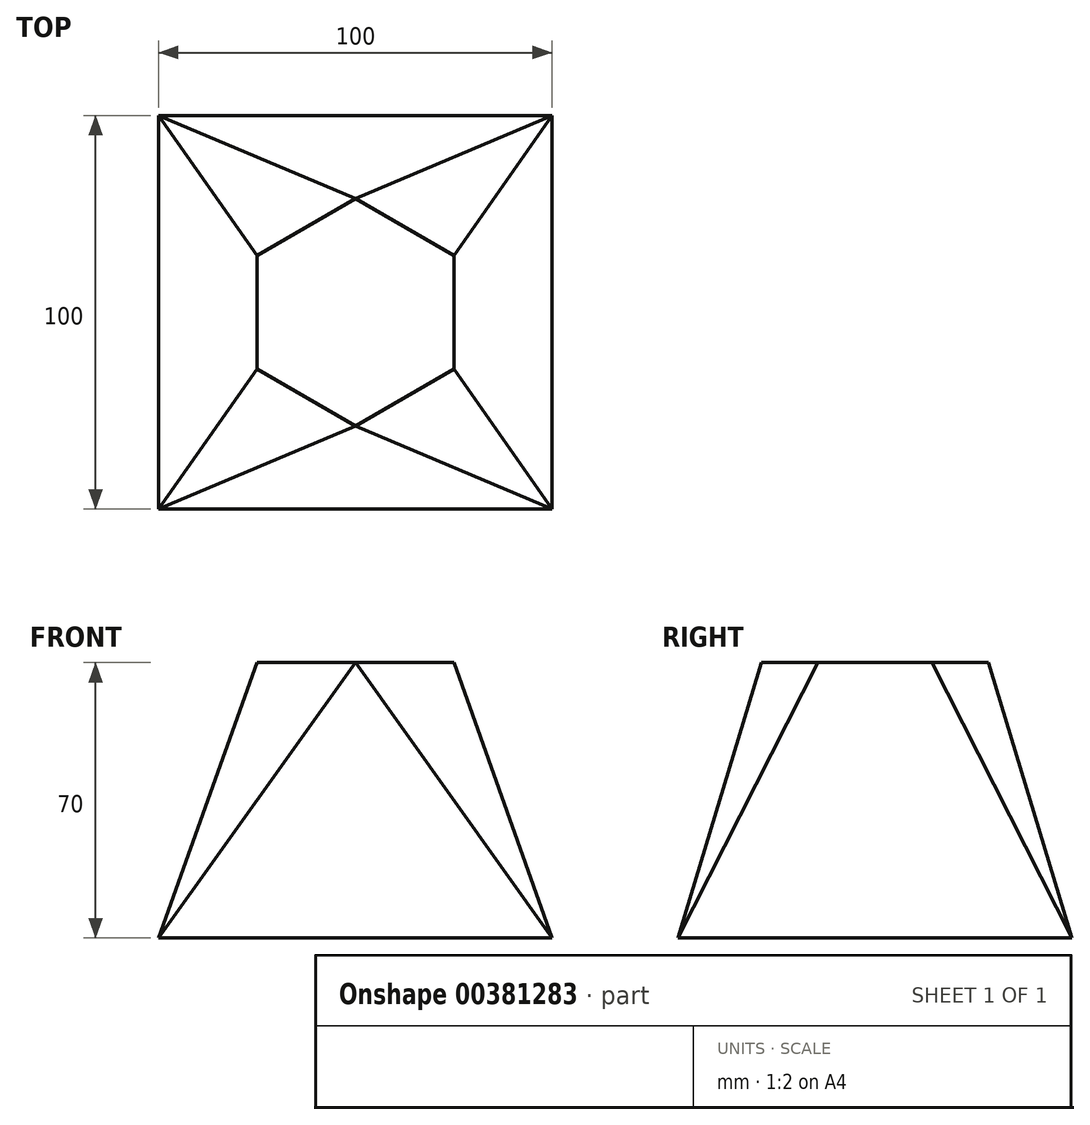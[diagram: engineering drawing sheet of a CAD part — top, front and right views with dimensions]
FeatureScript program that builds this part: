
annotation { "Feature Type Name" : "Feature", "Feature Type Description" : "" }
export const myFeature = defineFeature(function(context is Context, id is Id, definition is map)
    precondition{}
    {
        {
            var Q0;
            Q0=qCreatedBy(makeId("Top.planeOp"),FACE);
            var sketch = newSketch(context, id + "F0", { "sketchPlane" : qUnion([Q0])});
            skLineSegment(sketch, "E0.bottom", {"start": v(50, 50) * mm, "end": v(-50, 50) * mm});
            skLineSegment(sketch, "E0.top", {"start": v(50, -50) * mm, "end": v(-50, -50) * mm});
            skLineSegment(sketch, "E0.left", {"start": v(50, 50) * mm, "end": v(50, -50) * mm});
            skLineSegment(sketch, "E0.right", {"start": v(-50, 50) * mm, "end": v(-50, -50) * mm});
            skPoint(sketch, "E0.middle", {"position": v(0, 0) * mm});
            skSolve(sketch);
        }
        {
            var Q0;
            Q0=qCreatedBy(makeId("Top.planeOp"),FACE);
            cPlane(context, id + "F1", {"entities" : qUnion([Q0]), "cplaneType" : CPlaneType.OFFSET, "offset" : 70 * mm, "width" : 150 * mm, "height" : 150 * mm});
        }
        {
            var Q0;
            Q0=qCreatedBy(id+"F1.planeOp",FACE);
            var sketch = newSketch(context, id + "F2", { "sketchPlane" : qUnion([Q0])});
            skCircle(sketch, "E1.cCircle", {"center": v(0, 0) * mm, "radius": 25 * mm, "construction": true});
            skLineSegment(sketch, "E1.0", {"start": v(25, 14.43) * mm, "end": v(25, -14.43) * mm});
            skLineSegment(sketch, "E1.1", {"start": v(25, -14.43) * mm, "end": v(0, -28.87) * mm});
            skLineSegment(sketch, "E1.2", {"start": v(0, -28.87) * mm, "end": v(-25, -14.43) * mm});
            skLineSegment(sketch, "E1.3", {"start": v(-25, -14.43) * mm, "end": v(-25, 14.43) * mm});
            skLineSegment(sketch, "E1.4", {"start": v(-25, 14.43) * mm, "end": v(0, 28.87) * mm});
            skLineSegment(sketch, "E1.5", {"start": v(0, 28.87) * mm, "end": v(25, 14.43) * mm});
            skPoint(sketch, "E1.0.midPoint", {"position": v(25, 0) * mm});
            skLineSegment(sketch, "E2.bottom", {"start": v(25, -28.87) * mm, "end": v(-25, -28.87) * mm});
            skLineSegment(sketch, "E2.top", {"start": v(25, 28.87) * mm, "end": v(-25, 28.87) * mm});
            skLineSegment(sketch, "E2.left", {"start": v(25, -28.87) * mm, "end": v(25, 28.87) * mm});
            skLineSegment(sketch, "E2.right", {"start": v(-25, -28.87) * mm, "end": v(-25, 28.87) * mm});
            skSolve(sketch);
        }
        {
            var Q0;
            Q0=qCreatedBy(id+"F1.planeOp",FACE);
            var sketch = newSketch(context, id + "F3", { "sketchPlane" : qUnion([Q0])});
            skLineSegment(sketch, "E3.bottom", {"start": v(25, 28.87) * mm, "end": v(-25, 28.87) * mm});
            skLineSegment(sketch, "E3.top", {"start": v(25, -28.87) * mm, "end": v(-25, -28.87) * mm});
            skLineSegment(sketch, "E3.left", {"start": v(25, 28.87) * mm, "end": v(25, -28.87) * mm});
            skLineSegment(sketch, "E3.right", {"start": v(-25, 28.87) * mm, "end": v(-25, -28.87) * mm});
            skPoint(sketch, "E3.middle", {"position": v(0, 0) * mm});
            skSolve(sketch);
        }
        {
            var Q0;
            Q0=makeQuery(id+"F3.imprint","IMPRINT",FACE,{"disambiguationData":[TD([[makeQuery(id+"F3.imprint","IMPRINT",EDGE,{"derivedFrom":sQuery(id+"F3.wireOp",EDGE,"E3.bottom")}),1.0]])]});
            var Q1;
            Q1=makeQuery(id+"F0.imprint","IMPRINT",FACE,{"disambiguationData":[TD([[makeQuery(id+"F0.imprint","IMPRINT",EDGE,{"derivedFrom":sQuery(id+"F0.wireOp",EDGE,"E0.bottom")}),1.0]])]});
            loft(context, id + "F4", {"sheetProfilesArray" : [{ "sheetProfileEntities" : qUnion([Q0]) }, { "sheetProfileEntities" : qUnion([Q1]) }]});
        }
        {
            var Q1;
            {var subQ0=sQuery(id+"F2.wireOp",EDGE,"E1.1");Q1=makeQuery(id+"F2.imprint","IMPRINT",FACE,{"disambiguationData":[TD([[makeQuery(id+"F2.imprint","IMPRINT",EDGE,{"derivedFrom":subQ0}),1.0]])]});}
            var Q2;
            Q2=makeQuery(id+"F4.opLoft","MID_CAP_VERTEX",VERTEX,{"disambiguationData":[OSD([sQuery(id+"F0.wireOp",EDGE,"E0.top"),sQuery(id+"F0.wireOp",EDGE,"E0.left")])],"capPos":1.0});
            loft(context, id + "F5", {"sheetProfilesArray" : [{ "sheetProfileEntities" : qUnion([Q1]) }, { "sheetProfileEntities" : qUnion([Q2]) }]});
        }
        {
            var Q1;
            {var subQ0=sQuery(id+"F2.wireOp",EDGE,"E1.5");Q1=makeQuery(id+"F2.imprint","IMPRINT",FACE,{"disambiguationData":[TD([[makeQuery(id+"F2.imprint","IMPRINT",EDGE,{"derivedFrom":subQ0}),1.0]])]});}
            var Q2;
            Q2=makeQuery(id+"F4.opLoft","MID_CAP_VERTEX",VERTEX,{"disambiguationData":[OSD([sQuery(id+"F0.wireOp",EDGE,"E0.bottom"),sQuery(id+"F0.wireOp",EDGE,"E0.left")])],"capPos":1.0});
            loft(context, id + "F6", {"sheetProfilesArray" : [{ "sheetProfileEntities" : qUnion([Q1]) }, { "sheetProfileEntities" : qUnion([Q2]) }]});
        }
        {
            var Q1;
            {var subQ0=sQuery(id+"F2.wireOp",EDGE,"E1.2");Q1=makeQuery(id+"F2.imprint","IMPRINT",FACE,{"disambiguationData":[TD([[makeQuery(id+"F2.imprint","IMPRINT",EDGE,{"derivedFrom":subQ0}),1.0]])]});}
            var Q2;
            Q2=makeQuery(id+"F4.opLoft","MID_CAP_VERTEX",VERTEX,{"disambiguationData":[OSD([sQuery(id+"F0.wireOp",EDGE,"E0.top"),sQuery(id+"F0.wireOp",EDGE,"E0.right")])],"capPos":1.0});
            loft(context, id + "F7", {"sheetProfilesArray" : [{ "sheetProfileEntities" : qUnion([Q1]) }, { "sheetProfileEntities" : qUnion([Q2]) }]});
        }
        {
            var Q1;
            {var subQ0=sQuery(id+"F2.wireOp",EDGE,"E1.4");Q1=makeQuery(id+"F2.imprint","IMPRINT",FACE,{"disambiguationData":[TD([[makeQuery(id+"F2.imprint","IMPRINT",EDGE,{"derivedFrom":subQ0}),1.0]])]});}
            var Q2;
            Q2=makeQuery(id+"F4.opLoft","MID_CAP_VERTEX",VERTEX,{"disambiguationData":[OSD([sQuery(id+"F0.wireOp",EDGE,"E0.bottom"),sQuery(id+"F0.wireOp",EDGE,"E0.right")])],"capPos":1.0});
            loft(context, id + "F8", {"sheetProfilesArray" : [{ "sheetProfileEntities" : qUnion([Q1]) }, { "sheetProfileEntities" : qUnion([Q2]) }]});
        }
        {
            var Q0;
            {var subQ0=sQuery(id+"F2.wireOp",EDGE,"E1.1");Q0=makeQuery(id+"F5.opLoft","SWEPT_BODY",BODY,{"disambiguationData":[OSD([sQuery(id+"F0.wireOp",EDGE,"E0.top"),sQuery(id+"F0.wireOp",EDGE,"E0.left"),makeQuery(id+"F2.imprint","IMPRINT",FACE,{"disambiguationData":[TD([[makeQuery(id+"F2.imprint","IMPRINT",EDGE,{"derivedFrom":subQ0}),1.0]])]})])]});}
            var Q1;
            {var subQ0=sQuery(id+"F2.wireOp",EDGE,"E1.5");Q1=makeQuery(id+"F6.opLoft","SWEPT_BODY",BODY,{"disambiguationData":[OSD([sQuery(id+"F0.wireOp",EDGE,"E0.bottom"),sQuery(id+"F0.wireOp",EDGE,"E0.left"),makeQuery(id+"F2.imprint","IMPRINT",FACE,{"disambiguationData":[TD([[makeQuery(id+"F2.imprint","IMPRINT",EDGE,{"derivedFrom":subQ0}),1.0]])]})])]});}
            var Q2;
            {var subQ0=sQuery(id+"F2.wireOp",EDGE,"E1.2");Q2=makeQuery(id+"F7.opLoft","SWEPT_BODY",BODY,{"disambiguationData":[OSD([sQuery(id+"F0.wireOp",EDGE,"E0.top"),sQuery(id+"F0.wireOp",EDGE,"E0.right"),makeQuery(id+"F2.imprint","IMPRINT",FACE,{"disambiguationData":[TD([[makeQuery(id+"F2.imprint","IMPRINT",EDGE,{"derivedFrom":subQ0}),1.0]])]})])]});}
            var Q3;
            {var subQ0=sQuery(id+"F2.wireOp",EDGE,"E1.4");Q3=makeQuery(id+"F8.opLoft","SWEPT_BODY",BODY,{"disambiguationData":[OSD([sQuery(id+"F0.wireOp",EDGE,"E0.bottom"),sQuery(id+"F0.wireOp",EDGE,"E0.right"),makeQuery(id+"F2.imprint","IMPRINT",FACE,{"disambiguationData":[TD([[makeQuery(id+"F2.imprint","IMPRINT",EDGE,{"derivedFrom":subQ0}),1.0]])]})])]});}
            var Q4;
            Q4=makeQuery(id+"F4.opLoft","SWEPT_BODY",BODY,{"disambiguationData":[OSD([makeQuery(id+"F0.imprint","IMPRINT",FACE,{"disambiguationData":[TD([[makeQuery(id+"F0.imprint","IMPRINT",EDGE,{"derivedFrom":sQuery(id+"F0.wireOp",EDGE,"E0.bottom")}),1.0]])]}),makeQuery(id+"F3.imprint","IMPRINT",FACE,{"disambiguationData":[TD([[makeQuery(id+"F3.imprint","IMPRINT",EDGE,{"derivedFrom":sQuery(id+"F3.wireOp",EDGE,"E3.bottom")}),1.0]])]})])]});
            booleanBodies(context, id + "F9", {"operationType" : BooleanOperationType.SUBTRACTION, "tools" : qUnion([Q0, Q1, Q2, Q3]), "targets" : qUnion([Q4])});
        }
    });
